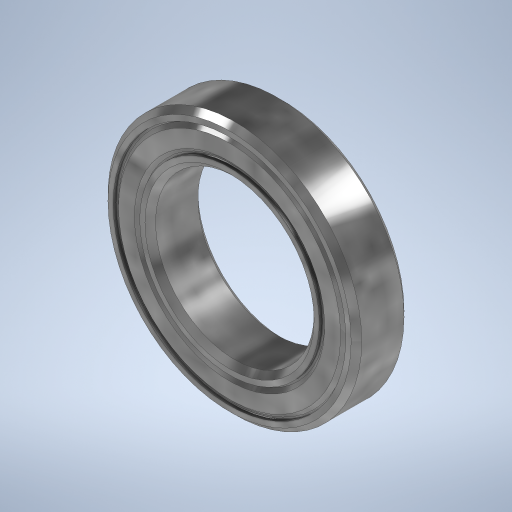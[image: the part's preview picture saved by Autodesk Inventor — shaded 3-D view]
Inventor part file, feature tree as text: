
AUTODESK INVENTOR PART (.ipt)
format: ipt  version: 2023.1 (Build 271208000, 208)  size: 384,512 bytes
history: native  units: mm
features: sketch x2, other x1, extrude x1, chamfer x1, revolve x1
ambient origin geometry x8: Origin, YZ Plane, XZ Plane, XY Plane, X Axis, Y Axis, Z Axis, Center Point
bodies: Body1 (feature_tree)
feature tree (6):
  other  "솔리드1"
  extrude  "돌출1"  Depth=15.0mm
  chamfer  "모따기1"  Distance=24.0mm
  revolve  "회전1"
  sketch  "스케치1"
  sketch  "스케치2"
